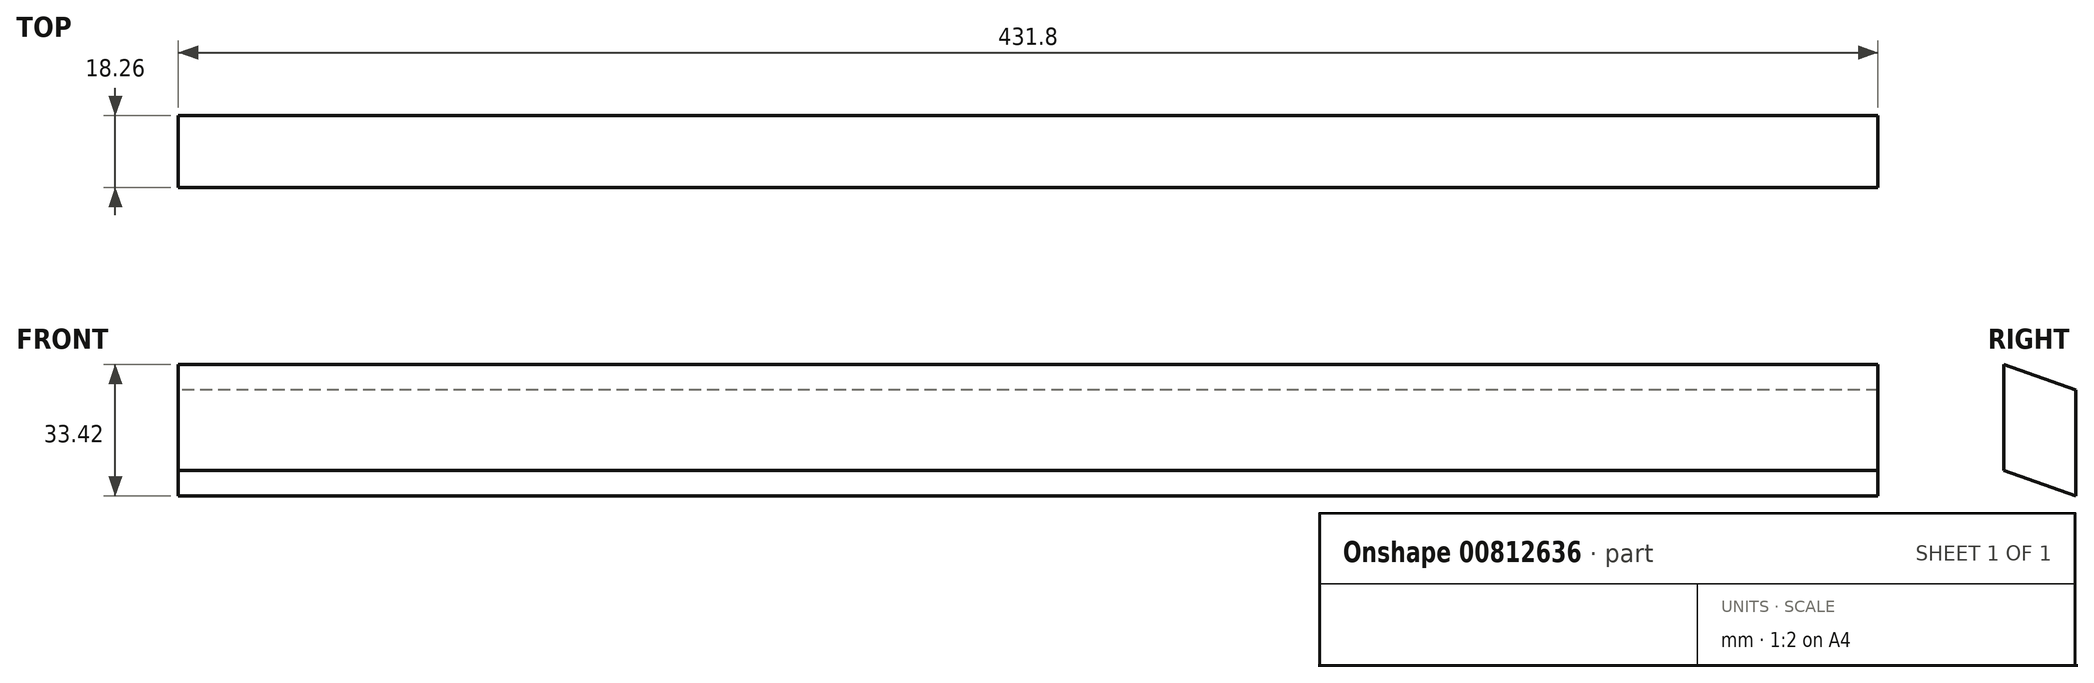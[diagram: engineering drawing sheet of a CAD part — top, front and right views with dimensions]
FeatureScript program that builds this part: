
annotation { "Feature Type Name" : "Feature", "Feature Type Description" : "" }
export const myFeature = defineFeature(function(context is Context, id is Id, definition is map)
    precondition{}
    {
        {
            var Q0;
            Q0=qCreatedBy(makeId("Right.planeOp"),FACE);
            var sketch = newSketch(context, id + "F0", { "sketchPlane" : qUnion([Q0])});
            skLineSegment(sketch, "E0", {"start": v(-140.85, 19.98) * mm, "end": v(-140.85, -81.62) * mm});
            skLineSegment(sketch, "E1", {"start": v(-140.85, -81.62) * mm, "end": v(145.7, -81.62) * mm});
            skLineSegment(sketch, "E2", {"start": v(145.7, -81.62) * mm, "end": v(-140.85, 19.98) * mm});
            skSolve(sketch);
        }
        {
            var Q0;
            Q0=qCreatedBy(makeId("Right.planeOp"),FACE);
            var sketch = newSketch(context, id + "F1", { "sketchPlane" : qUnion([Q0])});
            skLineSegment(sketch, "E3", {"start": v(-8.34, 14.4) * mm, "end": v(-8.34, -12.56) * mm});
            skLineSegment(sketch, "E4", {"start": v(-8.34, -12.56) * mm, "end": v(9.92, -19.03) * mm});
            skLineSegment(sketch, "E5", {"start": v(9.92, -19.03) * mm, "end": v(9.92, 7.92) * mm});
            skLineSegment(sketch, "E6", {"start": v(9.92, 7.92) * mm, "end": v(-8.34, 14.4) * mm});
            skSolve(sketch);
        }
        {
            var Q0;
            Q0=qSketchRegion(id+"F1",true);
            extrude(context, id + "F2", {"entities" : qUnion([Q0]), "depth" : 431.8 * mm, "offsetDistance" : 25.4 * mm});
        }
    });
